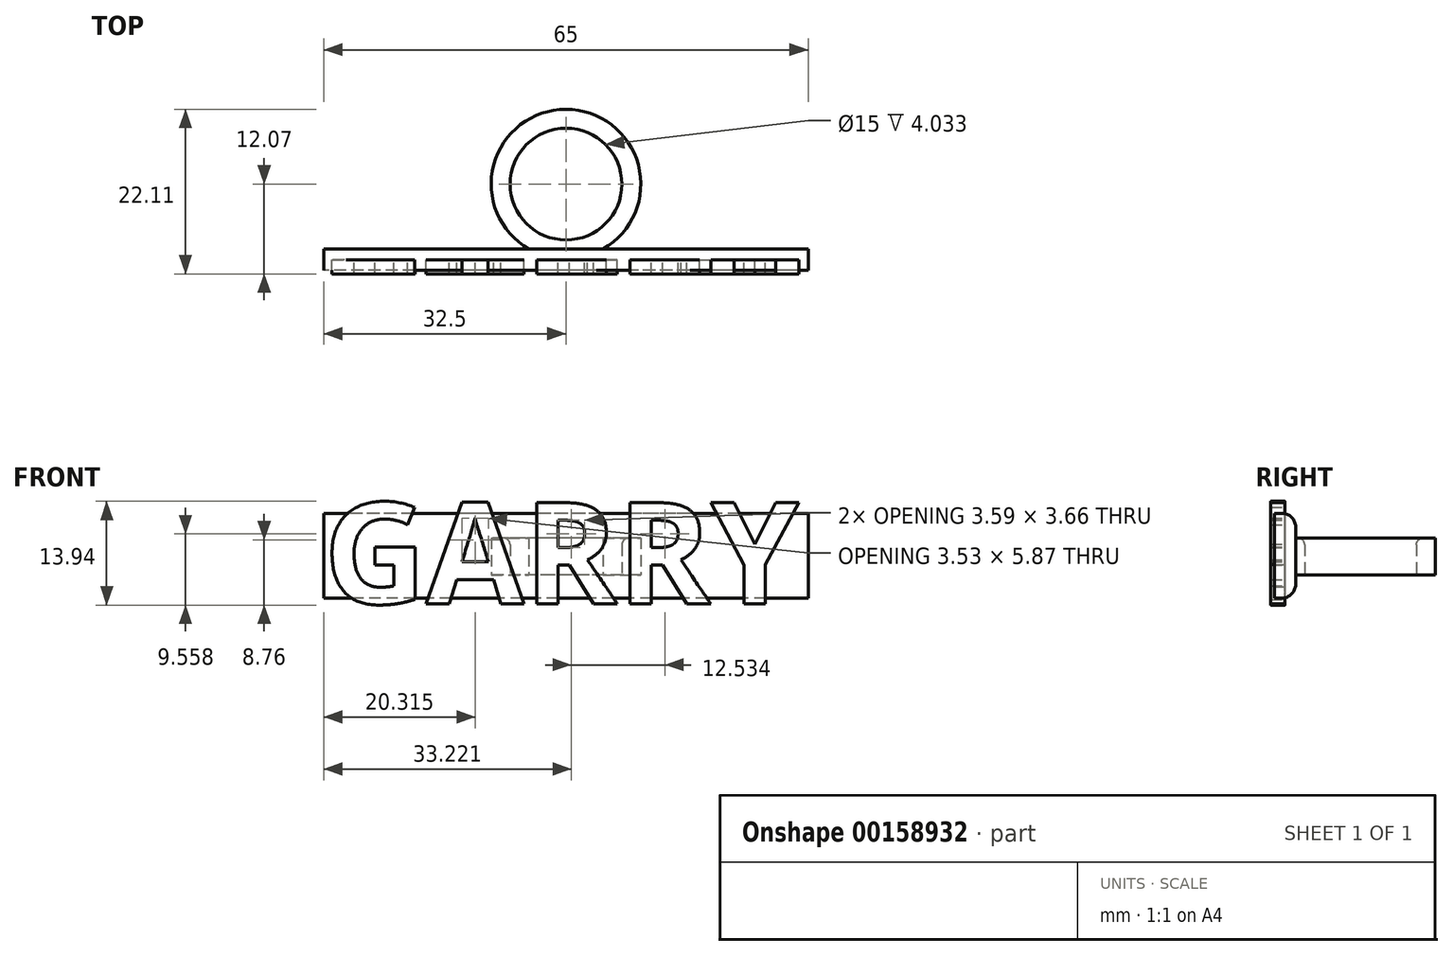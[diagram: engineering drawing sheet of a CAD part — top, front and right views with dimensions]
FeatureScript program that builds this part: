
annotation { "Feature Type Name" : "Feature", "Feature Type Description" : "" }
export const myFeature = defineFeature(function(context is Context, id is Id, definition is map)
    precondition{}
    {
        {
            var Q0;
            Q0=qCreatedBy(makeId("Front.planeOp"),FACE);
            cPlane(context, id + "F0", {"entities" : qUnion([Q0]), "cplaneType" : CPlaneType.OFFSET, "offset" : 10.16 * mm, "width" : 152.4 * mm, "height" : 152.4 * mm});
        }
        {
            var Q0;
            Q0=qCreatedBy(makeId("Top.planeOp"),FACE);
            var sketch = newSketch(context, id + "F1", { "sketchPlane" : qUnion([Q0])});
            skCircle(sketch, "E0", {"center": v(0, 0) * mm, "radius": 7.5 * mm});
            skCircle(sketch, "E1", {"center": v(0, 0) * mm, "radius": 10.04 * mm});
            skSolve(sketch);
        }
        {
            var Q0;
            Q0=makeQuery(id+"F1.imprint","IMPRINT",FACE,{"disambiguationData":[TD([[makeQuery(id+"F1.imprint","IMPRINT",EDGE,{"derivedFrom":sQuery(id+"F1.wireOp",EDGE,"E0")}),-1.0]])]});
            extrude(context, id + "F2", {"entities" : qUnion([Q0]), "endBound" : BoundingType.SYMMETRIC, "depth" : 4.95 * mm});
        }
        {
            var Q0;
            Q0=qCreatedBy(id+"F0.planeOp",FACE);
            var sketch = newSketch(context, id + "F3", { "sketchPlane" : qUnion([Q0])});
            skText(sketch, "E2", { "text": "GARRY", "fontName": "OpenSans-Bold.ttf"});
            const initialGuessF3  = {"E2": [-0.0325, -0.00634, 1, 0, 0.01367]};
            skSetInitialGuess(sketch, initialGuessF3);
            skSolve(sketch);
        }
        {
            var Q0;
            Q0=qCreatedBy(makeId("Right.planeOp"),FACE);
            var sketch = newSketch(context, id + "F4", { "sketchPlane" : qUnion([Q0])});
            skLineSegment(sketch, "E3.bottom", {"start": v(-8.72, 5.8) * mm, "end": v(-11.58, 5.8) * mm});
            skLineSegment(sketch, "E3.top", {"start": v(-8.72, -5.59) * mm, "end": v(-11.58, -5.59) * mm});
            skLineSegment(sketch, "E3.left", {"start": v(-8.72, 5.8) * mm, "end": v(-8.72, -5.59) * mm});
            skLineSegment(sketch, "E3.right", {"start": v(-11.58, 5.8) * mm, "end": v(-11.58, -5.59) * mm});
            skSolve(sketch);
        }
        {
            var Q0;
            Q0 = qSketchRegion(id + "F4", true);
            extrude(context, id + "F5", {"entities" : qUnion([Q0]), "operationType" : NewBodyOperationType.ADD, "endBound" : BoundingType.SYMMETRIC, "depth" : 65 * mm});
        }
        {
            var Q0;
            Q0 = qSketchRegion(id + "F3", true);
            extrude(context, id + "F6", {"entities" : qUnion([Q0]), "depth" : 1.9 * mm});
        }
        {
            var Q0;
            Q0=makeQuery(id+"F2.opExtrude","CAP_EDGE",EDGE,{"disambiguationData":[OSD([sQuery(id+"F1.wireOp",EDGE,"E0")])],"isStart":false});
            fillet(context, id + "F7", {"entities" : qUnion([Q0]), "radius" : 0.92 * mm, "tangentPropagation" : true, "allowEdgeOverflow" : false});
        }
        {
            var Q0;
            Q0=makeQuery(id+"F5.opExtrude","SWEPT_EDGE",EDGE,{"disambiguationData":[OSD([sQuery(id+"F4.wireOp",EDGE,"E3.top"),sQuery(id+"F4.wireOp",EDGE,"E3.left")])]});
            var Q1;
            Q1=makeQuery(id+"F5.opExtrude","SWEPT_EDGE",EDGE,{"disambiguationData":[OSD([sQuery(id+"F4.wireOp",EDGE,"E3.bottom"),sQuery(id+"F4.wireOp",EDGE,"E3.left")])]});
            fillet(context, id + "F8", {"entities" : qUnion([Q0, Q1]), "radius" : 1.84 * mm, "tangentPropagation" : true, "allowEdgeOverflow" : false});
        }
    });
